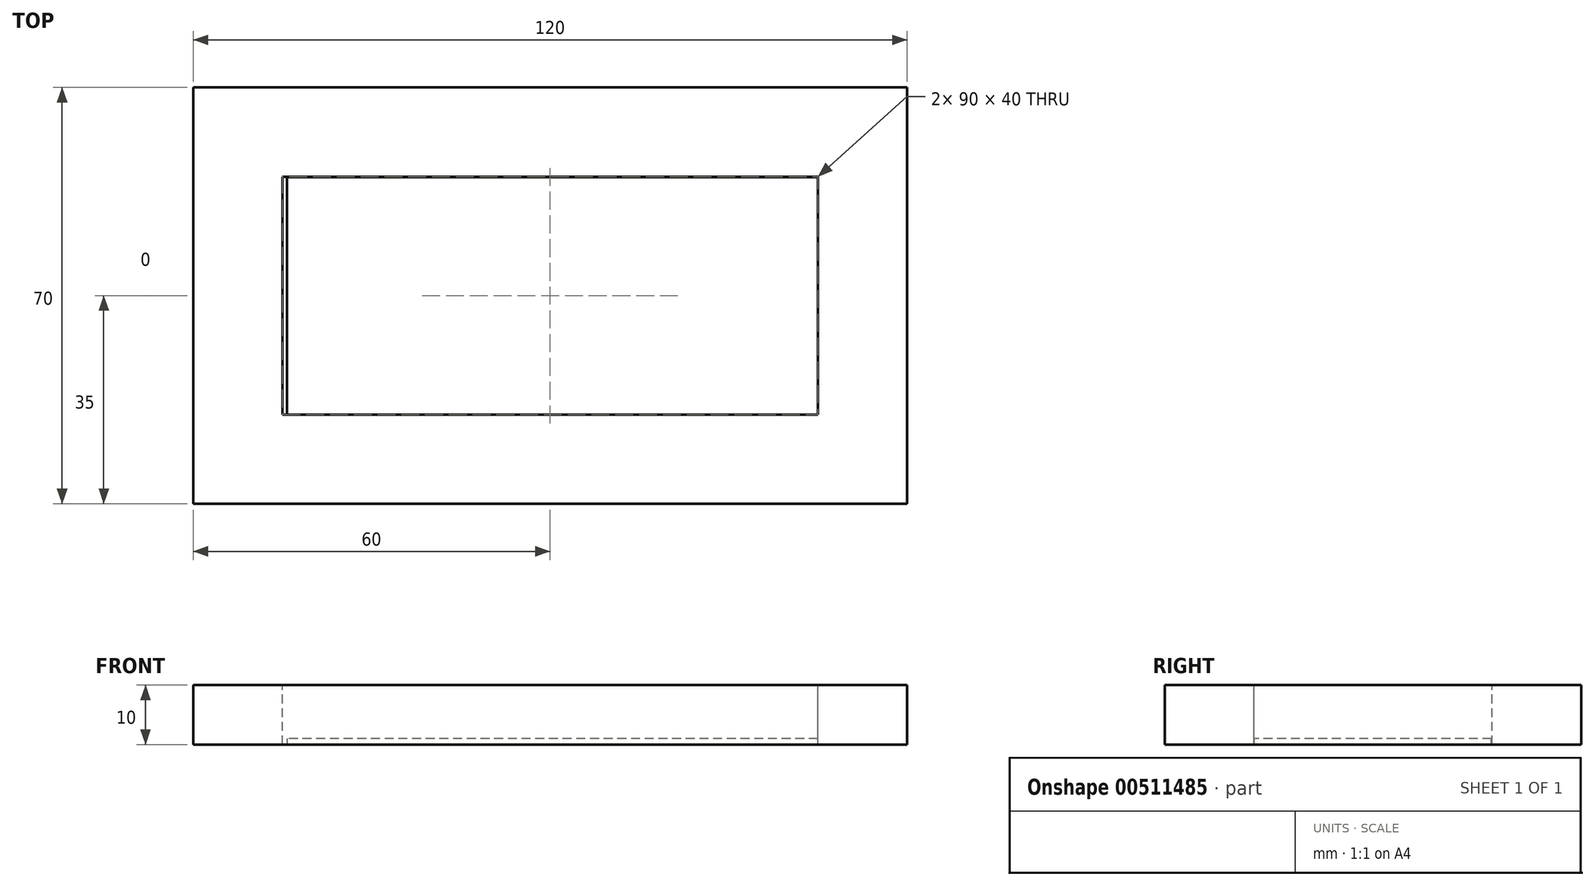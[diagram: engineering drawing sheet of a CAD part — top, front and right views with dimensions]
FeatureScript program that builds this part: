
annotation { "Feature Type Name" : "Feature", "Feature Type Description" : "" }
export const myFeature = defineFeature(function(context is Context, id is Id, definition is map)
    precondition{}
    {
        {
            var Q0;
            Q0=qCreatedBy(makeId("Top.planeOp"),FACE);
            var sketch = newSketch(context, id + "F0", { "sketchPlane" : qUnion([Q0])});
            skLineSegment(sketch, "E0", {"start": v(0, 0) * mm, "end": v(0, 70) * mm});
            skLineSegment(sketch, "E1", {"start": v(0, 70) * mm, "end": v(120, 70) * mm});
            skLineSegment(sketch, "E2", {"start": v(120, 70) * mm, "end": v(120, 0) * mm});
            skLineSegment(sketch, "E3", {"start": v(120, 0) * mm, "end": v(0, 0) * mm});
            skSolve(sketch);
        }
        {
            var Q0;
            Q0=makeQuery(id+"F0.imprint","IMPRINT",FACE,{"disambiguationData":[TD([[makeQuery(id+"F0.imprint","IMPRINT",EDGE,{"derivedFrom":sQuery(id+"F0.wireOp",EDGE,"E0")}),-1.0]])]});
            extrude(context, id + "F1", {"entities" : qUnion([Q0]), "depth" : 10 * mm});
        }
        {
            var Q0;
            Q0=makeQuery(id+"F1.opExtrude","CAP_FACE",FACE,{"disambiguationData":[OSD([sQuery(id+"F0.wireOp",EDGE,"E0"),sQuery(id+"F0.wireOp",EDGE,"E1"),sQuery(id+"F0.wireOp",EDGE,"E2"),sQuery(id+"F0.wireOp",EDGE,"E3")])],"isStart":false});
            var sketch = newSketch(context, id + "F2", { "sketchPlane" : qUnion([Q0])});
            skLineSegment(sketch, "E4", {"start": v(18.5, 0) * mm, "end": v(18.5, 15) * mm});
            skLineSegment(sketch, "E5", {"start": v(18.5, 15) * mm, "end": v(105, 15) * mm});
            skLineSegment(sketch, "E6", {"start": v(105, 15) * mm, "end": v(105, 55) * mm});
            skLineSegment(sketch, "E7", {"start": v(105, 55) * mm, "end": v(15, 55) * mm});
            skLineSegment(sketch, "E8", {"start": v(15, 55) * mm, "end": v(15, 15) * mm});
            skLineSegment(sketch, "E9", {"start": v(15, 15) * mm, "end": v(18.5, 15) * mm});
            skSolve(sketch);
        }
        {
            var Q0;
            Q0=makeQuery(id+"F2.imprint","IMPRINT",FACE,{"disambiguationData":[TD([[makeQuery(id+"F2.imprint","IMPRINT",EDGE,{"derivedFrom":sQuery(id+"F2.wireOp",EDGE,"E5")}),1.0]])]});
            extrude(context, id + "F3", {"entities" : qUnion([Q0]), "operationType" : NewBodyOperationType.REMOVE, "oppositeDirection" : true, "depth" : 25 * mm});
        }
        {
            var Q0;
            Q0=qCreatedBy(makeId("Top.planeOp"),FACE);
            var sketch = newSketch(context, id + "F4", { "sketchPlane" : qUnion([Q0])});
            skLineSegment(sketch, "E10", {"start": v(15.76, 54.9) * mm, "end": v(105.76, 54.9) * mm});
            skLineSegment(sketch, "E11", {"start": v(105.76, 54.9) * mm, "end": v(105.76, 14.9) * mm});
            skLineSegment(sketch, "E12", {"start": v(105.76, 14.9) * mm, "end": v(15.76, 14.9) * mm});
            skLineSegment(sketch, "E13", {"start": v(15.76, 14.9) * mm, "end": v(15.76, 54.9) * mm});
            skSolve(sketch);
        }
        {
            var Q0;
            Q0=makeQuery(id+"F4.imprint","IMPRINT",FACE,{"disambiguationData":[TD([[makeQuery(id+"F4.imprint","IMPRINT",EDGE,{"derivedFrom":sQuery(id+"F4.wireOp",EDGE,"E10")}),-1.0]])]});
            var sketch = newSketch(context, id + "F5", { "sketchPlane" : qUnion([Q0])});
            skSolve(sketch);
        }
        {
            var Q0;
            Q0 = qSketchRegion(id + "F4", true);
            extrude(context, id + "F6", {"entities" : qUnion([Q0]), "operationType" : NewBodyOperationType.ADD, "depth" : 1 * mm});
        }
        {
            var Q0;
            Q0=makeQuery(id+"F5.imprint","IMPRINT",FACE,{"disambiguationData":[TD([[makeQuery(id+"F5.imprint","IMPRINT",EDGE,{"derivedFrom":makeQuery(id+"F4.imprint","IMPRINT",EDGE,{"derivedFrom":sQuery(id+"F4.wireOp",EDGE,"E10")})}),-1.0]])]});
            extrude(context, id + "F7", {"entities" : qUnion([Q0]), "operationType" : NewBodyOperationType.ADD, "depth" : 1 * mm});
        }
        {
            var Q0;
            Q0=makeQuery(id+"F1.opExtrude","SWEPT_BODY",BODY,{"disambiguationData":[OSD([sQuery(id+"F0.wireOp",EDGE,"E0"),sQuery(id+"F0.wireOp",EDGE,"E1"),sQuery(id+"F0.wireOp",EDGE,"E2"),sQuery(id+"F0.wireOp",EDGE,"E3")])]});
            transform(context, id + "F8", {"entities" : qUnion([Q0]), "transformType" : TransformType.TRANSLATION_3D, "dx" : 0 * mm, "dy" : 0 * mm, "dz" : 0 * mm, "makeCopy" : true});
        }
    });
